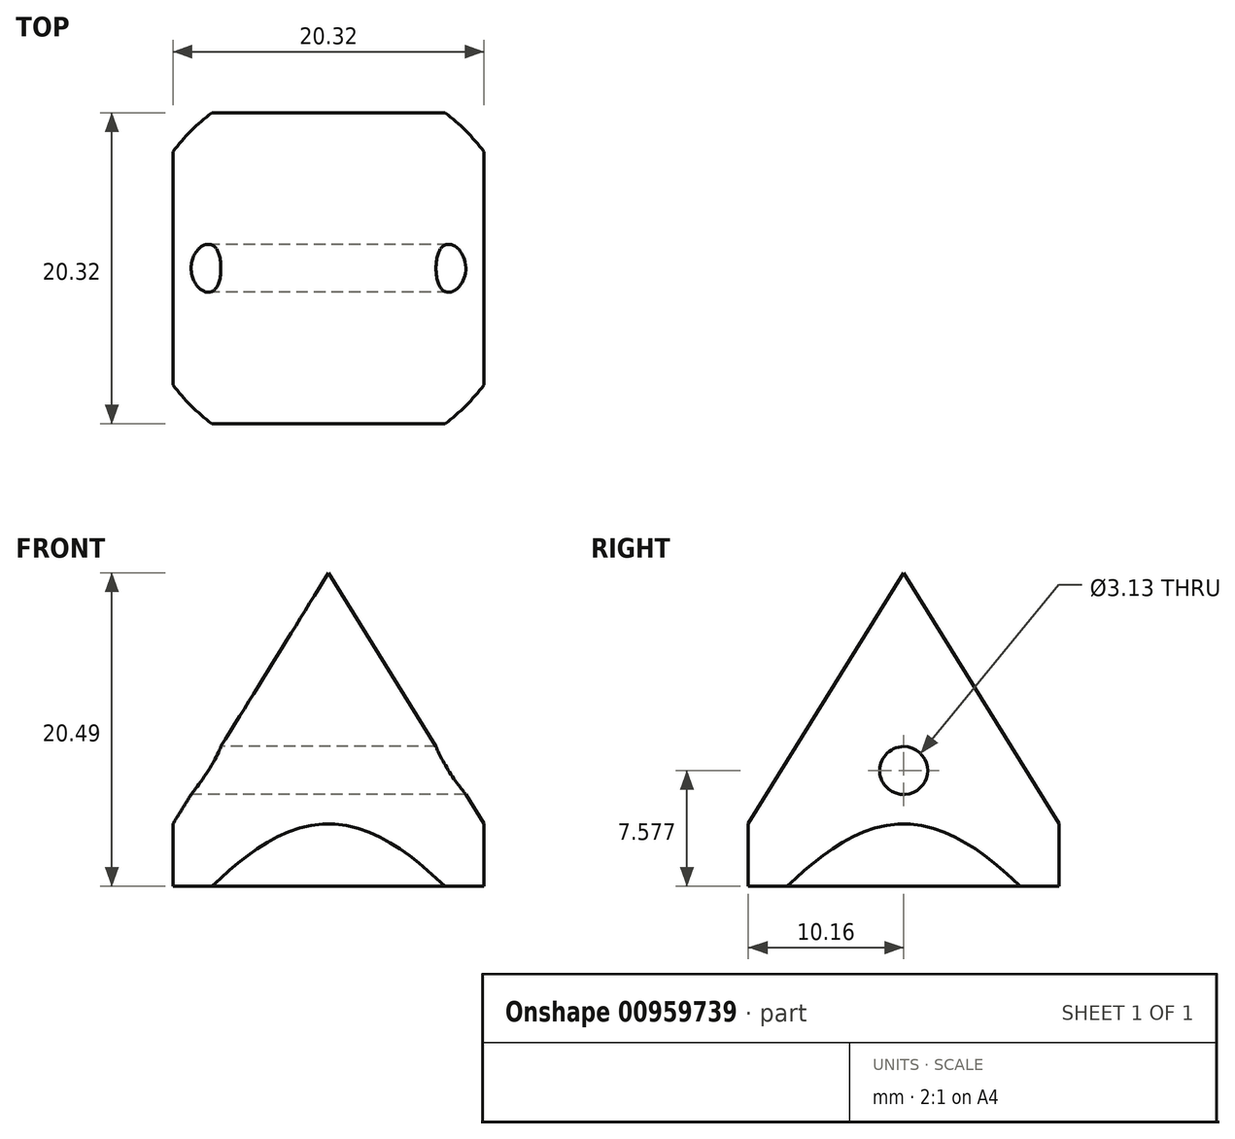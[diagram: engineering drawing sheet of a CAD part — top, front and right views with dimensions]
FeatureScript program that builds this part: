
annotation { "Feature Type Name" : "Feature", "Feature Type Description" : "" }
export const myFeature = defineFeature(function(context is Context, id is Id, definition is map)
    precondition{}
    {
        {
            var Q0;
            Q0=qCreatedBy(makeId("Front.planeOp"),FACE);
            var sketch = newSketch(context, id + "F0", { "sketchPlane" : qUnion([Q0])});
            skLineSegment(sketch, "E0", {"start": v(0, 0) * mm, "end": v(-12.7, 0) * mm});
            skLineSegment(sketch, "E1", {"start": v(-12.7, 0) * mm, "end": v(0, 20.49) * mm});
            skLineSegment(sketch, "E2", {"start": v(0, 20.49) * mm, "end": v(0, 0) * mm});
            skSolve(sketch);
        }
        {
            var Q0;
            Q0=qCreatedBy(makeId("Front.planeOp"),FACE);
            var sketch = newSketch(context, id + "F1", { "sketchPlane" : qUnion([Q0])});
            skLineSegment(sketch, "E3", {"start": v(0, 35.22) * mm, "end": v(0, 48.26) * mm});
            skSolve(sketch);
        }
        {
            var Q0;
            Q0 = qSketchRegion(id + "F0", true);
            var Q1;
            Q1=sQuery(id+"F1.wireOp",EDGE,"E3");
            revolve(context, id + "F2", {"surfaceOperationType" : NewSurfaceOperationType.NEW, "entities" : qUnion([Q0]), "axis" : qUnion([Q1]), "revolveType" : RevolveType.FULL});
        }
        {
            var Q0;
            Q0=qCreatedBy(makeId("Top.planeOp"),FACE);
            var sketch = newSketch(context, id + "F3", { "sketchPlane" : qUnion([Q0])});
            skLineSegment(sketch, "E4.bottom", {"start": v(8.87, 10.16) * mm, "end": v(-8.87, 10.16) * mm});
            skLineSegment(sketch, "E4.top", {"start": v(8.87, -10.16) * mm, "end": v(-8.87, -10.16) * mm});
            skLineSegment(sketch, "E4.left", {"start": v(10.16, 8.87) * mm, "end": v(10.16, -8.87) * mm});
            skLineSegment(sketch, "E4.right", {"start": v(-10.16, 8.87) * mm, "end": v(-10.16, -8.87) * mm});
            skPoint(sketch, "E4.middle", {"position": v(0, 0) * mm});
            skArc(sketch, "E5", {"start": v(-10.16, 8.87) * mm, "mid": v(-13.49, 0) * mm, "end": v(-10.16, -8.87) * mm});
            skPoint(sketch, "E6.orphan", {"position": v(-10.16, -10.16) * mm});
            skPoint(sketch, "E7.orphan", {"position": v(10.16, -10.16) * mm});
            skPoint(sketch, "E8.orphan", {"position": v(10.16, 10.16) * mm});
            skPoint(sketch, "E9.orphan", {"position": v(-10.16, 10.16) * mm});
            skArc(sketch, "E10.trimOffspring", {"start": v(8.87, 10.16) * mm, "mid": v(0, 13.49) * mm, "end": v(-8.87, 10.16) * mm});
            skArc(sketch, "E11.trimOffspring", {"start": v(10.16, -8.87) * mm, "mid": v(13.49, 0) * mm, "end": v(10.16, 8.87) * mm});
            skArc(sketch, "E12.trimOffspring", {"start": v(-8.87, -10.16) * mm, "mid": v(0, -13.49) * mm, "end": v(8.87, -10.16) * mm});
            skSolve(sketch);
        }
        {
            var Q0;
            Q0 = qSketchRegion(id + "F3", true);
            extrude(context, id + "F4", {"entities" : qUnion([Q0]), "operationType" : NewBodyOperationType.REMOVE, "depth" : 25.4 * mm, "offsetDistance" : 25.4 * mm});
        }
        {
            var Q0;
            Q0=qCreatedBy(makeId("Right.planeOp"),FACE);
            var sketch = newSketch(context, id + "F5", { "sketchPlane" : qUnion([Q0])});
            skCircle(sketch, "E13", {"center": v(0, 7.58) * mm, "radius": 1.57 * mm});
            skSolve(sketch);
        }
        {
            var Q0;
            Q0 = qSketchRegion(id + "F5", true);
            extrude(context, id + "F6", {"entities" : qUnion([Q0]), "operationType" : NewBodyOperationType.REMOVE, "endBound" : BoundingType.SYMMETRIC, "depth" : 25.4 * mm, "offsetDistance" : 25.4 * mm});
        }
    });
